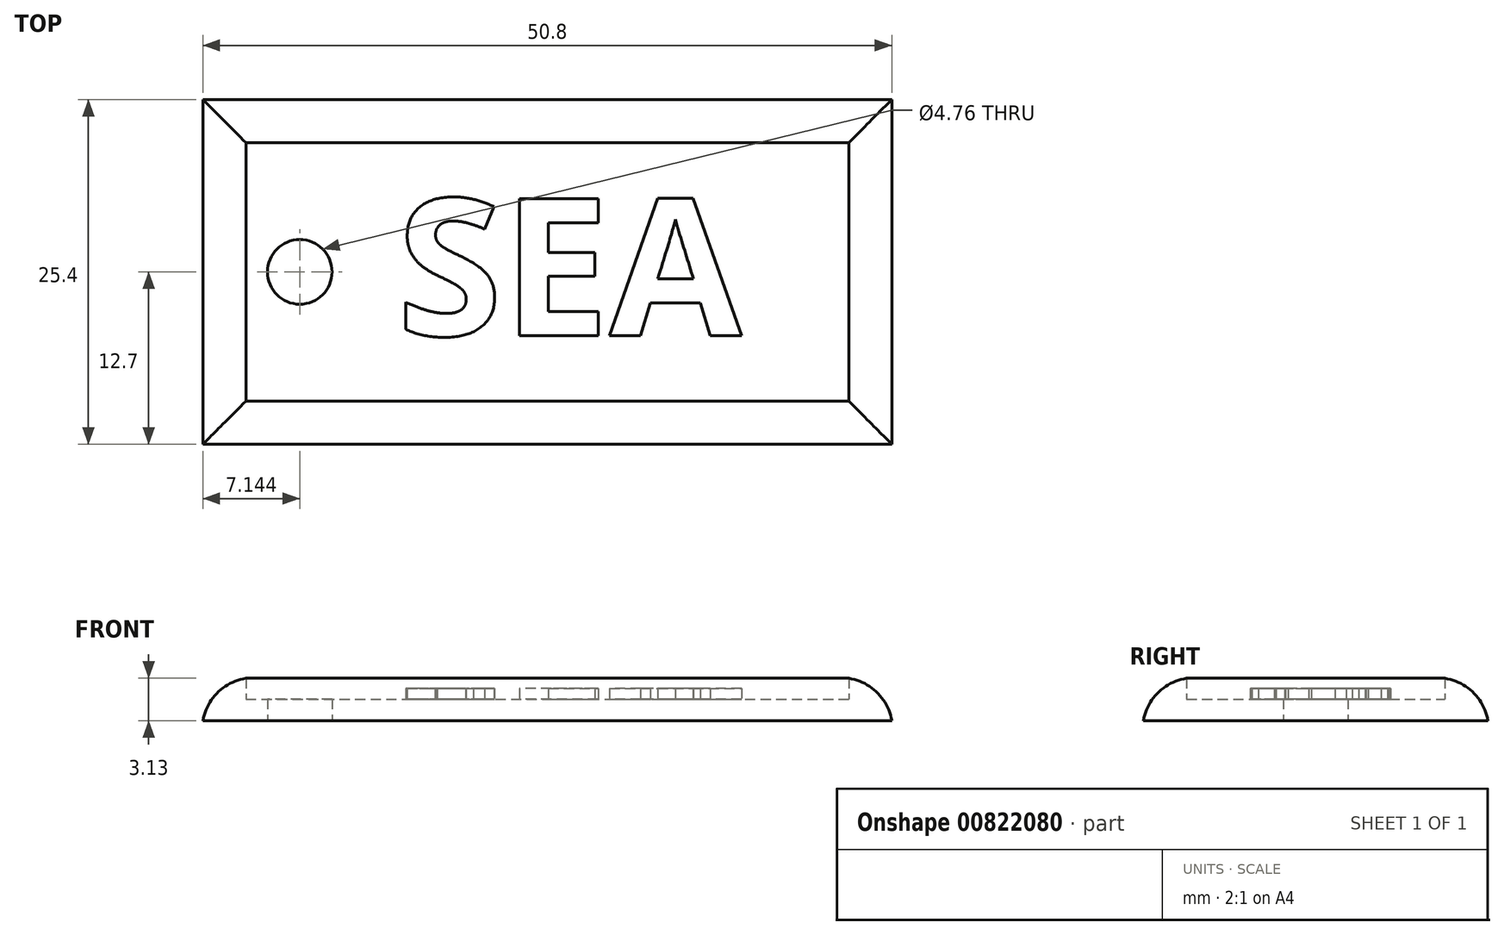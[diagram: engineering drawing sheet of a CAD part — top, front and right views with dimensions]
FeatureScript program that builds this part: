
annotation { "Feature Type Name" : "Feature", "Feature Type Description" : "" }
export const myFeature = defineFeature(function(context is Context, id is Id, definition is map)
    precondition{}
    {
        {
            var Q0;
            Q0=qCreatedBy(makeId("Top.planeOp"),FACE);
            var sketch = newSketch(context, id + "F0", { "sketchPlane" : qUnion([Q0])});
            skLineSegment(sketch, "E0.bottom", {"start": v(0, 0) * mm, "end": v(50.8, 0) * mm});
            skLineSegment(sketch, "E0.top", {"start": v(0, 25.4) * mm, "end": v(50.8, 25.4) * mm});
            skLineSegment(sketch, "E0.left", {"start": v(0, 0) * mm, "end": v(0, 25.4) * mm});
            skLineSegment(sketch, "E0.right", {"start": v(50.8, 0) * mm, "end": v(50.8, 25.4) * mm});
            skCircle(sketch, "E1", {"center": v(7.14, 12.7) * mm, "radius": 2.38 * mm});
            skPoint(sketch, "E1.centerSnap0", {"position": v(0, 12.7) * mm});
            skLineSegment(sketch, "E2.0", {"start": v(3.17, 3.18) * mm, "end": v(3.17, 22.22) * mm});
            skLineSegment(sketch, "E2.1", {"start": v(3.18, 3.18) * mm, "end": v(47.62, 3.18) * mm});
            skLineSegment(sketch, "E2.2", {"start": v(47.62, 3.18) * mm, "end": v(47.62, 22.23) * mm});
            skLineSegment(sketch, "E2.3", {"start": v(3.17, 22.23) * mm, "end": v(47.62, 22.23) * mm});
            skSolve(sketch);
        }
        {
            var Q0;
            Q0=makeQuery(id+"F0.imprint","IMPRINT",FACE,{"disambiguationData":[TD([[makeQuery(id+"F0.imprint","IMPRINT",EDGE,{"derivedFrom":sQuery(id+"F0.wireOp",EDGE,"E1")}),-1.0]])]});
            extrude(context, id + "F1", {"entities" : qUnion([Q0]), "depth" : 1.59 * mm, "offsetDistance" : 25.4 * mm});
        }
        {
            var Q0;
            Q0 = qSketchRegion(id + "F0", true);
            extrude(context, id + "F2", {"entities" : qUnion([Q0]), "operationType" : NewBodyOperationType.ADD, "depth" : 3.17 * mm, "offsetDistance" : 25.4 * mm});
        }
        {
            var Q0;
            Q0=makeQuery(id+"F1.opExtrude","CAP_FACE",FACE,{"disambiguationData":[OSD([sQuery(id+"F0.wireOp",EDGE,"E1"),sQuery(id+"F0.wireOp",EDGE,"E2.0"),sQuery(id+"F0.wireOp",EDGE,"E2.1"),sQuery(id+"F0.wireOp",EDGE,"E2.2"),sQuery(id+"F0.wireOp",EDGE,"E2.3")])],"isStart":false});
            var sketch = newSketch(context, id + "F3", { "sketchPlane" : qUnion([Q0])});
            skText(sketch, "E3", { "text": "SEA", "fontName": "OpenSans-Bold.ttf"});
            const initialGuessF3  = {"E3": [0.0143, 0.00801, 1, 0, 0.01016]};
            skSetInitialGuess(sketch, initialGuessF3);
            skSolve(sketch);
        }
        {
            var Q0;
            Q0=qCreatedBy(makeId("Top.planeOp"),FACE);
            var sketch = newSketch(context, id + "F4", { "sketchPlane" : qUnion([Q0])});
            skSolve(sketch);
        }
        {
            var Q0;
            Q0 = qSketchRegion(id + "F4", true);
            var Q1;
            Q1 = qSketchRegion(id + "F3", true);
            extrude(context, id + "F5", {"entities" : qUnion([Q0, Q1]), "operationType" : NewBodyOperationType.ADD, "depth" : 0.8 * mm, "offsetDistance" : 25.4 * mm});
        }
        {
            var Q0;
            Q0=makeQuery(id+"F2.opExtrude","CAP_EDGE",EDGE,{"disambiguationData":[OSD([sQuery(id+"F0.wireOp",EDGE,"E0.bottom")])],"isStart":false});
            var Q1;
            Q1=makeQuery(id+"F2.opExtrude","CAP_EDGE",EDGE,{"disambiguationData":[OSD([sQuery(id+"F0.wireOp",EDGE,"E0.left")])],"isStart":false});
            var Q2;
            Q2=makeQuery(id+"F2.opExtrude","CAP_EDGE",EDGE,{"disambiguationData":[OSD([sQuery(id+"F0.wireOp",EDGE,"E0.top")])],"isStart":false});
            var Q3;
            Q3=makeQuery(id+"F2.opExtrude","CAP_EDGE",EDGE,{"disambiguationData":[OSD([sQuery(id+"F0.wireOp",EDGE,"E0.right")])],"isStart":false});
            fillet(context, id + "F6", {"entities" : qUnion([Q0, Q1, Q2, Q3]), "radius" : 3.8 * mm, "tangentPropagation" : true, "allowEdgeOverflow" : false});
        }
    });
